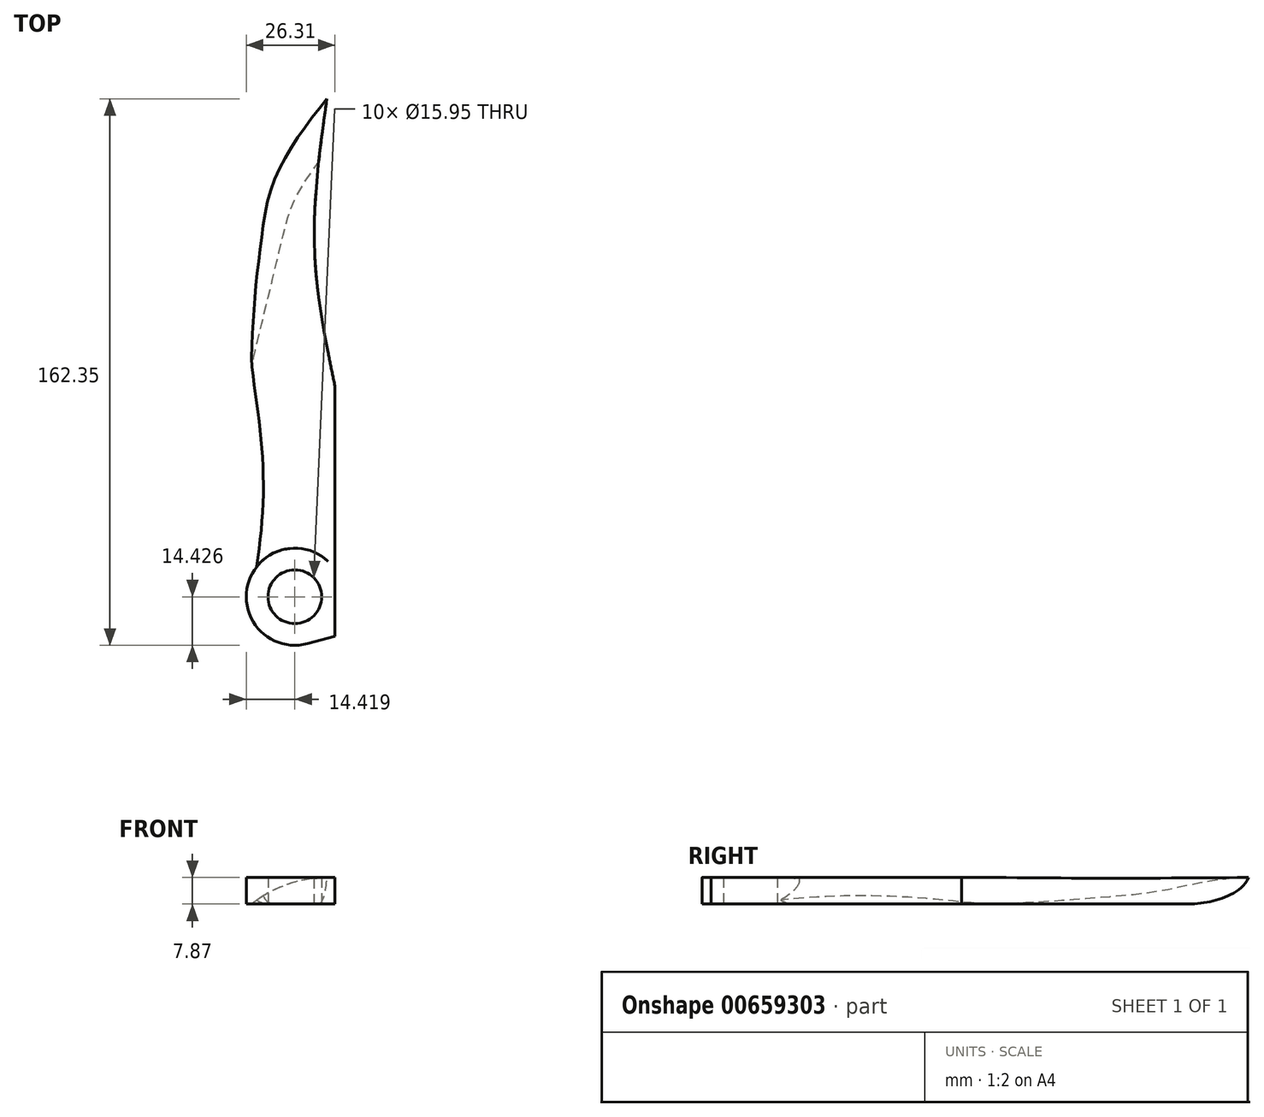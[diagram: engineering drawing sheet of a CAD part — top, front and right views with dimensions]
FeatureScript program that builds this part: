
annotation { "Feature Type Name" : "Feature", "Feature Type Description" : "" }
export const myFeature = defineFeature(function(context is Context, id is Id, definition is map)
    precondition{}
    {
        {
            var Q0;
            Q0=qCreatedBy(makeId("Top.planeOp"),FACE);
            var sketch = newSketch(context, id + "F0", { "sketchPlane" : qUnion([Q0])});
            skArc(sketch, "E0", {"start": v(0, -56.23) * mm, "mid": v(3.34, -29.6) * mm, "end": v(0, -2.98) * mm});
            skArc(sketch, "E1", {"start": v(0, -56.23) * mm, "mid": v(1.73, -71.8) * mm, "end": v(16.64, -76.61) * mm});
            skLineSegment(sketch, "E2", {"start": v(16.64, -76.61) * mm, "end": v(24.8, -74.42) * mm});
            skLineSegment(sketch, "E3", {"start": v(24.8, -74.42) * mm, "end": v(24.8, 0) * mm});
            skLineSegment(sketch, "E4", {"start": v(24.8, 0) * mm, "end": v(0, -2.98) * mm});
            skLineSegment(sketch, "E5", {"start": v(0, -2.98) * mm, "end": v(0, 47.35) * mm});
            skFitSpline(sketch, "E6", {"points": [v(0, 47.35) * mm, v(4.58, 60.66) * mm, v(22.47, 85.62) * mm], "startDerivative": vector(7.58, 31.18) * mm, "endDerivative": vector(35.56, 44.5) * mm});
            skFitSpline(sketch, "E7", {"points": [v(22.47, 85.62) * mm, v(18.72, 41.1) * mm, v(24.8, 0) * mm], "startDerivative": vector(-12.37, -88.38) * mm, "endDerivative": vector(17.2, -82.82) * mm});
            skCircle(sketch, "E8", {"center": v(12.9, -62.68) * mm, "radius": 7.98 * mm});
            skSolve(sketch);
        }
        {
            var Q0;
            Q0=makeQuery(id+"F0.imprint","IMPRINT",FACE,{"disambiguationData":[TD([[makeQuery(id+"F0.imprint","IMPRINT",EDGE,{"derivedFrom":sQuery(id+"F0.wireOp",EDGE,"E4")}),-1.0]])]});
            var Q1;
            Q1=makeQuery(id+"F0.imprint","IMPRINT",FACE,{"disambiguationData":[TD([[makeQuery(id+"F0.imprint","IMPRINT",EDGE,{"derivedFrom":sQuery(id+"F0.wireOp",EDGE,"E0")}),-1.0]])]});
            extrude(context, id + "F1", {"entities" : qUnion([Q0, Q1]), "depth" : 7.87 * mm, "offsetDistance" : 25.4 * mm});
        }
        {
            var Q0;
            Q0=makeQuery(id+"F1.opExtrude","CAP_EDGE",EDGE,{"disambiguationData":[OSD([sQuery(id+"F0.wireOp",EDGE,"E5")])],"isStart":false});
            fillet(context, id + "F2", {"entities" : qUnion([Q0]), "radius" : 36.8 * mm, "tangentPropagation" : true, "allowEdgeOverflow" : false});
        }
        {
            var Q0;
            Q0=makeQuery(id+"F1.opExtrude","CAP_EDGE",EDGE,{"disambiguationData":[OSD([sQuery(id+"F0.wireOp",EDGE,"E6")])],"isStart":true});
            fillet(context, id + "F3", {"entities" : qUnion([Q0]), "radius" : 9.8 * mm, "tangentPropagation" : true, "allowEdgeOverflow" : false});
        }
        {
            var Q0;
            Q0=makeQuery(id+"F1.opExtrude","CAP_EDGE",EDGE,{"disambiguationData":[OSD([sQuery(id+"F0.wireOp",EDGE,"E0")])],"isStart":true});
            fillet(context, id + "F4", {"entities" : qUnion([Q0]), "radius" : 3.68 * mm, "tangentPropagation" : true, "allowEdgeOverflow" : false});
        }
    });
